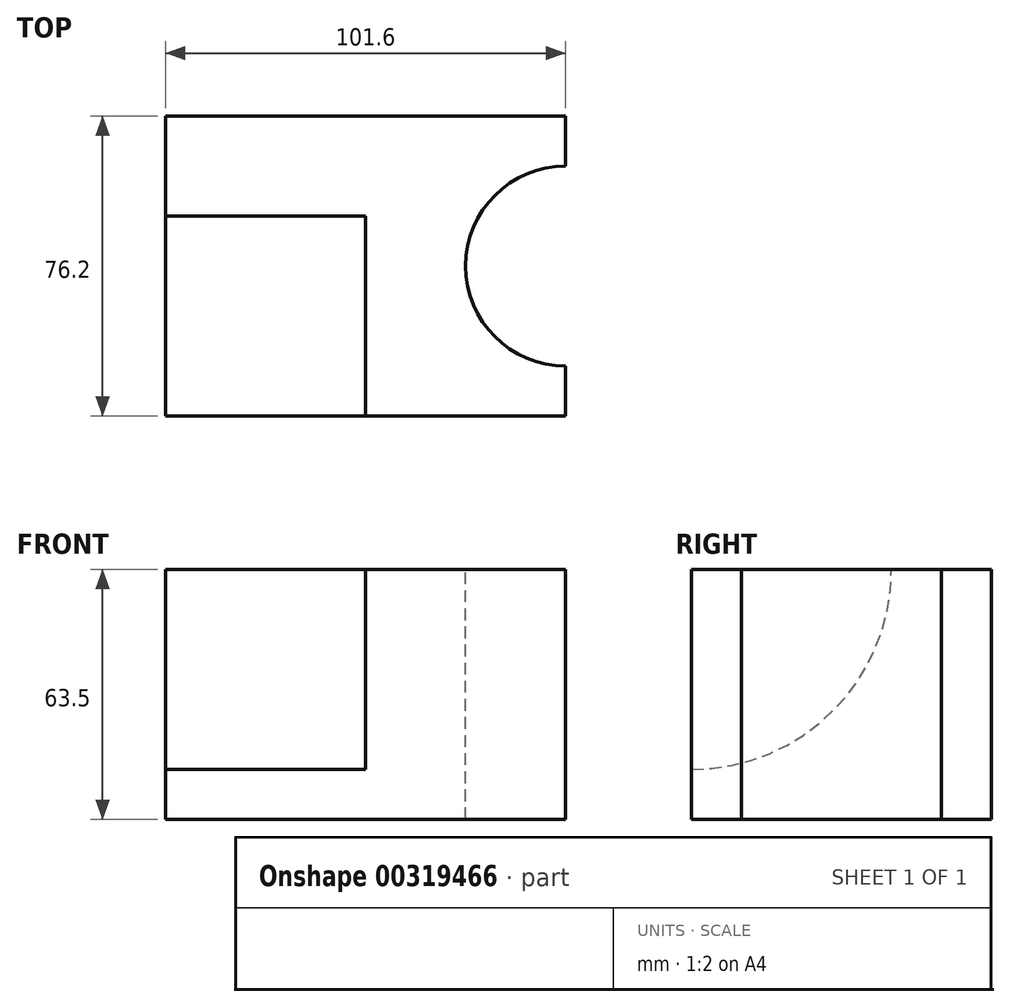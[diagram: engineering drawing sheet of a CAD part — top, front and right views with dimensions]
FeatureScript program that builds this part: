
annotation { "Feature Type Name" : "Feature", "Feature Type Description" : "" }
export const myFeature = defineFeature(function(context is Context, id is Id, definition is map)
    precondition{}
    {
        {
            var Q0;
            Q0=qCreatedBy(makeId("Front.planeOp"),FACE);
            var sketch = newSketch(context, id + "F0", { "sketchPlane" : qUnion([Q0])});
            skLineSegment(sketch, "E0.bottom", {"start": v(-55.46, 11.35) * mm, "end": v(46.14, 11.35) * mm});
            skLineSegment(sketch, "E0.top", {"start": v(-55.46, -52.15) * mm, "end": v(46.14, -52.15) * mm});
            skLineSegment(sketch, "E0.left", {"start": v(-55.46, 11.35) * mm, "end": v(-55.46, -52.15) * mm});
            skLineSegment(sketch, "E0.right", {"start": v(46.14, 11.35) * mm, "end": v(46.14, -52.15) * mm});
            skSolve(sketch);
        }
        {
            var Q0;
            Q0=makeQuery(id+"F0.imprint","IMPRINT",FACE,{"disambiguationData":[TD([[makeQuery(id+"F0.imprint","IMPRINT",EDGE,{"derivedFrom":sQuery(id+"F0.wireOp",EDGE,"E0.bottom")}),-1.0]])]});
            extrude(context, id + "F1", {"entities" : qUnion([Q0]), "depth" : 76.2 * mm});
        }
        {
            var Q0;
            Q0=makeQuery(id+"F1.opExtrude","SWEPT_FACE",FACE,{"disambiguationData":[OSD([sQuery(id+"F0.wireOp",EDGE,"E0.bottom")])]});
            var sketch = newSketch(context, id + "F2", { "sketchPlane" : qUnion([Q0])});
            skArc(sketch, "E1", {"start": v(46.14, -12.7) * mm, "mid": v(20.74, -38.1) * mm, "end": v(46.14, -63.5) * mm});
            skLineSegment(sketch, "E2", {"start": v(46.14, -12.7) * mm, "end": v(46.14, -63.5) * mm});
            skSolve(sketch);
        }
        {
            var Q0;
            Q0 = qSketchRegion(id + "F2", true);
            extrude(context, id + "F3", {"entities" : qUnion([Q0]), "operationType" : NewBodyOperationType.REMOVE, "endBound" : BoundingType.THROUGH_ALL, "oppositeDirection" : true, "depth" : 25.4 * mm});
        }
        {
            var Q0;
            Q0=makeQuery(id+"F1.opExtrude","SWEPT_FACE",FACE,{"disambiguationData":[OSD([sQuery(id+"F0.wireOp",EDGE,"E0.left")])]});
            var sketch = newSketch(context, id + "F4", { "sketchPlane" : qUnion([Q0])});
            skArc(sketch, "E3", {"start": v(25.4, 11.35) * mm, "mid": v(40.28, -24.57) * mm, "end": v(76.2, -39.45) * mm});
            skLineSegment(sketch, "E4", {"start": v(76.2, 11.35) * mm, "end": v(25.4, 11.35) * mm});
            skLineSegment(sketch, "E5", {"start": v(76.2, 11.35) * mm, "end": v(76.2, -39.45) * mm});
            skSolve(sketch);
        }
        {
            var Q0;
            Q0=makeQuery(id+"F4.imprint","IMPRINT",FACE,{"disambiguationData":[TD([[makeQuery(id+"F4.imprint","IMPRINT",EDGE,{"derivedFrom":sQuery(id+"F4.wireOp",EDGE,"E3")}),1.0]])]});
            extrude(context, id + "F5", {"entities" : qUnion([Q0]), "operationType" : NewBodyOperationType.REMOVE, "oppositeDirection" : true, "depth" : 50.8 * mm});
        }
    });
